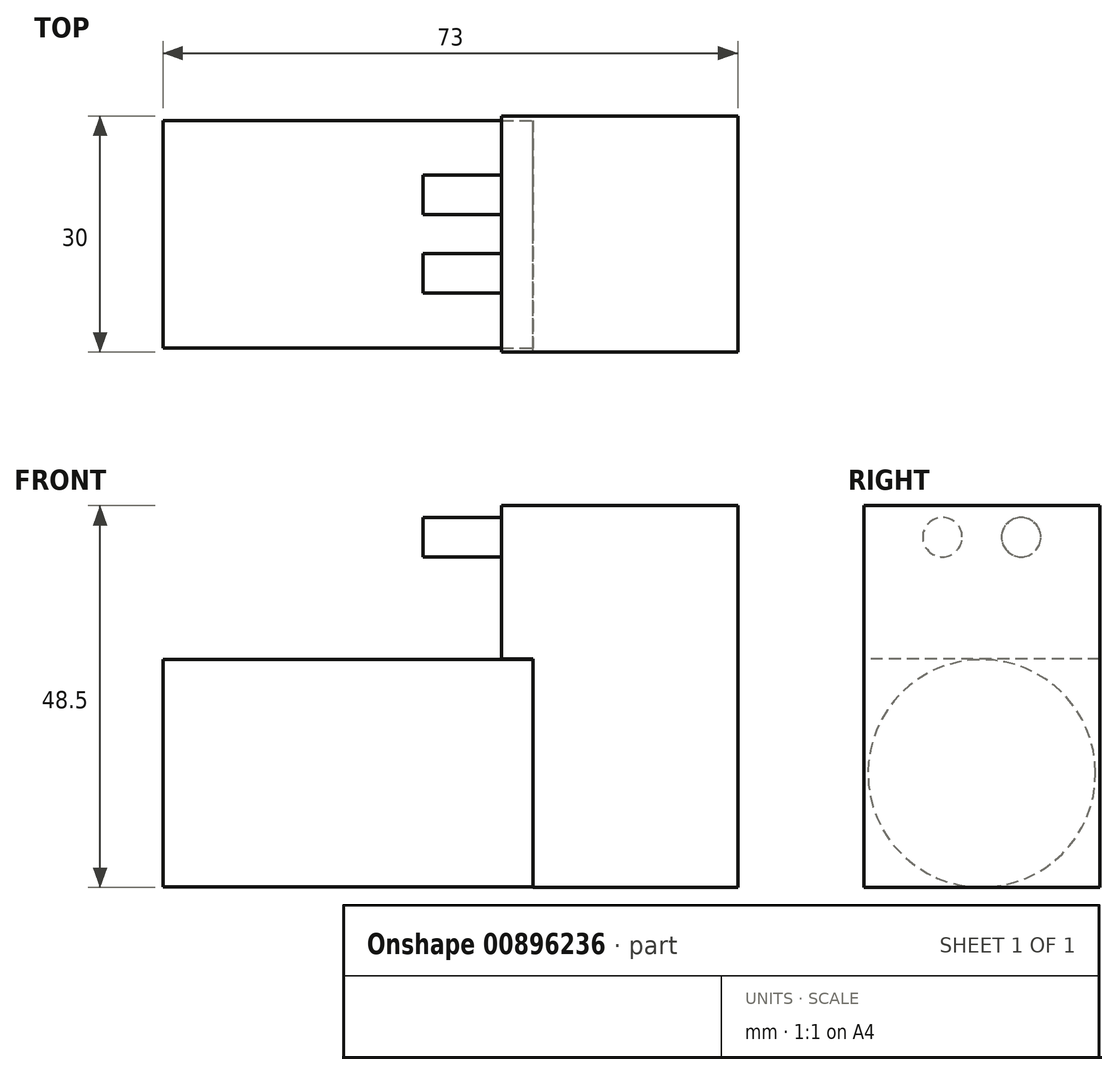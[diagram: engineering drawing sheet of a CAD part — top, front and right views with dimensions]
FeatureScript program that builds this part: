
annotation { "Feature Type Name" : "Feature", "Feature Type Description" : "" }
export const myFeature = defineFeature(function(context is Context, id is Id, definition is map)
    precondition{}
    {
        {
            var Q0;
            Q0=qCreatedBy(makeId("Top.planeOp"),FACE);
            var sketch = newSketch(context, id + "F0", { "sketchPlane" : qUnion([Q0])});
            skLineSegment(sketch, "E0.bottom", {"start": v(-15, 15) * mm, "end": v(15, 15) * mm});
            skLineSegment(sketch, "E0.top", {"start": v(-15, -15) * mm, "end": v(15, -15) * mm});
            skLineSegment(sketch, "E0.left", {"start": v(-15, 15) * mm, "end": v(-15, -15) * mm});
            skLineSegment(sketch, "E0.right", {"start": v(15, 15) * mm, "end": v(15, -15) * mm});
            skSolve(sketch);
        }
        {
            var Q0;
            Q0 = qSketchRegion(id + "F0", true);
            extrude(context, id + "F1", {"entities" : qUnion([Q0]), "depth" : 48.5 * mm, "offsetDistance" : 25 * mm});
        }
        {
            var Q0;
            Q0=makeQuery(id+"F1.opExtrude","CAP_FACE",FACE,{"disambiguationData":[OSD([sQuery(id+"F0.wireOp",EDGE,"E0.bottom"),sQuery(id+"F0.wireOp",EDGE,"E0.top"),sQuery(id+"F0.wireOp",EDGE,"E0.left"),sQuery(id+"F0.wireOp",EDGE,"E0.right")])],"isStart":true});
            var sketch = newSketch(context, id + "F2", { "sketchPlane" : qUnion([Q0])});
            skLineSegment(sketch, "E1.bottom", {"start": v(-15, 15) * mm, "end": v(-11, 15) * mm});
            skLineSegment(sketch, "E1.top", {"start": v(-15, -15) * mm, "end": v(-11, -15) * mm});
            skLineSegment(sketch, "E1.left", {"start": v(-15, 15) * mm, "end": v(-15, -15) * mm});
            skLineSegment(sketch, "E1.right", {"start": v(-11, 15) * mm, "end": v(-11, -15) * mm});
            skSolve(sketch);
        }
        {
            var Q0;
            Q0 = qSketchRegion(id + "F2", true);
            extrude(context, id + "F3", {"entities" : qUnion([Q0]), "operationType" : NewBodyOperationType.REMOVE, "oppositeDirection" : true, "depth" : 29 * mm, "offsetDistance" : 25 * mm});
        }
        {
            var Q0;
            Q0=makeQuery(id+"F3.boolean.opBoolean","COPY",FACE,{"derivedFrom":makeQuery(id+"F3.opExtrude","SWEPT_FACE",FACE,{"disambiguationData":[OSD([sQuery(id+"F2.wireOp",EDGE,"E1.right")])]})});
            var sketch = newSketch(context, id + "F4", { "sketchPlane" : qUnion([Q0])});
            skCircle(sketch, "E2", {"center": v(0, 14.5) * mm, "radius": 14.45 * mm});
            skSolve(sketch);
        }
        {
            var Q0;
            Q0 = qSketchRegion(id + "F4", true);
            extrude(context, id + "F5", {"entities" : qUnion([Q0]), "operationType" : NewBodyOperationType.ADD, "depth" : 47 * mm, "offsetDistance" : 25 * mm});
        }
        {
            var Q0;
            Q0=makeQuery(id+"F1.opExtrude","SWEPT_FACE",FACE,{"disambiguationData":[OSD([sQuery(id+"F0.wireOp",EDGE,"E0.left")])]});
            var sketch = newSketch(context, id + "F6", { "sketchPlane" : qUnion([Q0])});
            skLineSegment(sketch, "E3", {"start": v(-16.76, 44.5) * mm, "end": v(23.27, 44.5) * mm, "construction": true});
            skCircle(sketch, "E4", {"center": v(5, 44.5) * mm, "radius": 2.5 * mm});
            skCircle(sketch, "E5", {"center": v(-5, 44.5) * mm, "radius": 2.5 * mm});
            skSolve(sketch);
        }
        {
            var Q0;
            Q0 = qSketchRegion(id + "F6", true);
            extrude(context, id + "F7", {"entities" : qUnion([Q0]), "operationType" : NewBodyOperationType.ADD, "depth" : 10 * mm, "offsetDistance" : 25 * mm});
        }
    });
